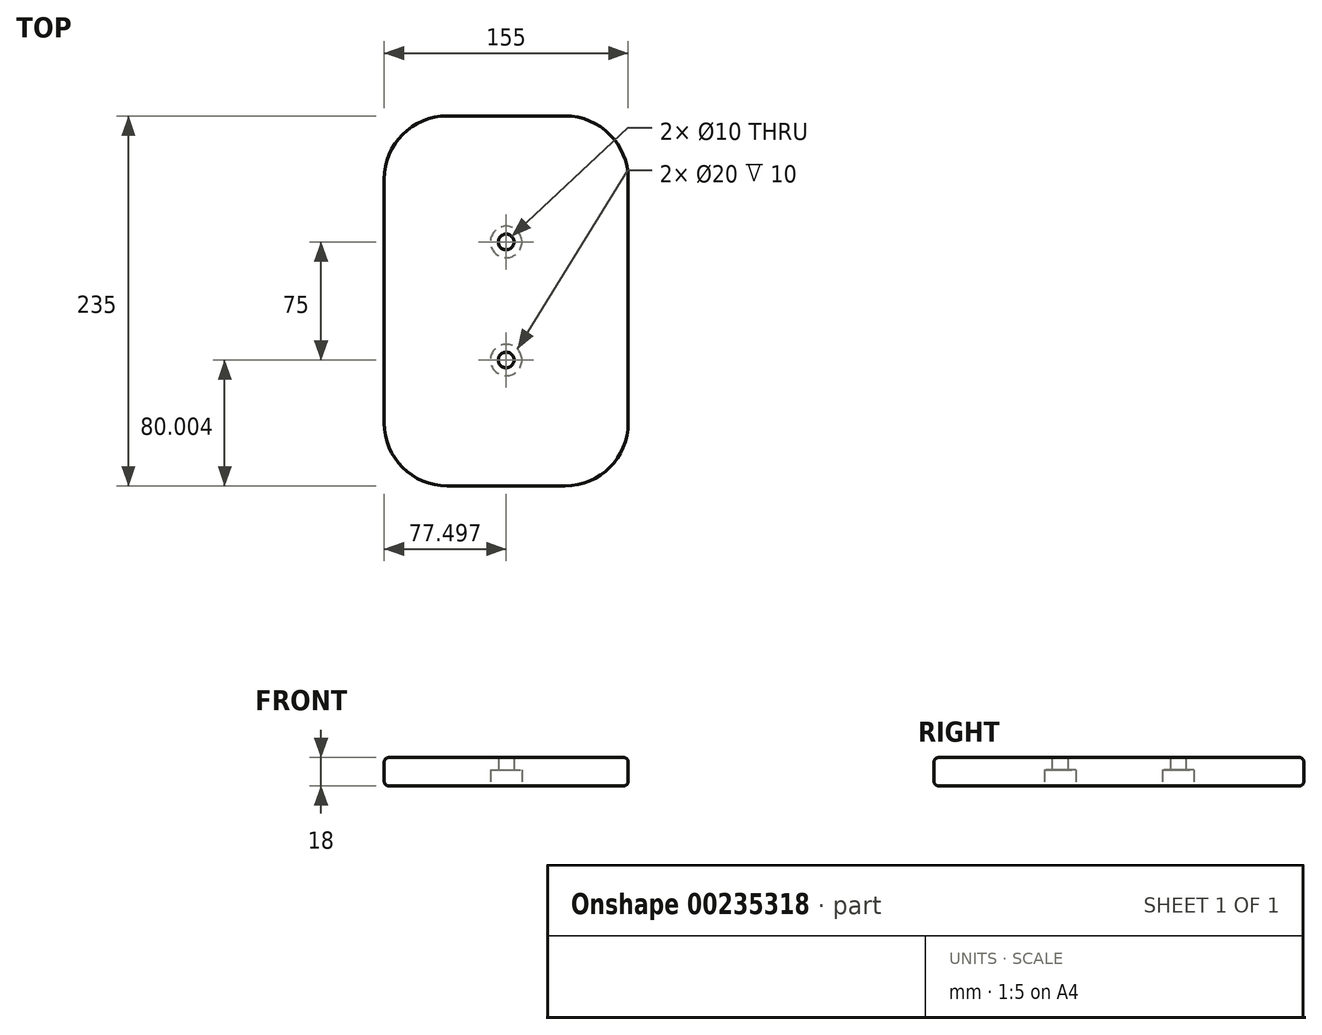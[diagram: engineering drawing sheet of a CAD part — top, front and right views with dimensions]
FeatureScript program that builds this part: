
annotation { "Feature Type Name" : "Feature", "Feature Type Description" : "" }
export const myFeature = defineFeature(function(context is Context, id is Id, definition is map)
    precondition{}
    {
        {
            var Q0;
            Q0=qCreatedBy(makeId("Top.planeOp"),FACE);
            var sketch = newSketch(context, id + "F0", { "sketchPlane" : qUnion([Q0])});
            skLineSegment(sketch, "E0.bottom", {"start": v(-32.73, -118.2) * mm, "end": v(42.27, -118.2) * mm});
            skLineSegment(sketch, "E0.top", {"start": v(-32.73, 116.8) * mm, "end": v(42.27, 116.8) * mm});
            skLineSegment(sketch, "E0.left", {"start": v(-72.73, -78.2) * mm, "end": v(-72.73, 76.8) * mm});
            skLineSegment(sketch, "E0.right", {"start": v(82.27, -78.2) * mm, "end": v(82.27, 76.8) * mm});
            skPoint(sketch, "E1.visualSharp", {"position": v(-72.73, 116.8) * mm});
            skArc(sketch, "E1.filletArc", {"start": v(-32.73, 116.8) * mm, "mid": v(-61.02, 105.09) * mm, "end": v(-72.73, 76.8) * mm});
            skPoint(sketch, "E2.visualSharp", {"position": v(82.27, 116.8) * mm});
            skArc(sketch, "E2.filletArc", {"start": v(82.27, 76.8) * mm, "mid": v(70.55, 105.09) * mm, "end": v(42.27, 116.8) * mm});
            skPoint(sketch, "E3.visualSharp", {"position": v(82.27, -118.2) * mm});
            skArc(sketch, "E3.filletArc", {"start": v(42.27, -118.2) * mm, "mid": v(70.55, -106.48) * mm, "end": v(82.27, -78.2) * mm});
            skPoint(sketch, "E4.visualSharp", {"position": v(-72.73, -118.2) * mm});
            skArc(sketch, "E4.filletArc", {"start": v(-72.73, -78.2) * mm, "mid": v(-61.02, -106.48) * mm, "end": v(-32.73, -118.2) * mm});
            skPoint(sketch, "E5.centerSnap0", {"position": v(-72.73, -0.7) * mm});
            skCircle(sketch, "E6", {"center": v(4.77, 36.8) * mm, "radius": 5 * mm});
            skPoint(sketch, "E6.centerSnap0", {"position": v(4.77, 116.8) * mm});
            skCircle(sketch, "E7", {"center": v(4.77, -38.2) * mm, "radius": 5 * mm});
            skSolve(sketch);
        }
        {
            var Q0;
            Q0=makeQuery(id+"F0.imprint","IMPRINT",FACE,{"disambiguationData":[TD([[makeQuery(id+"F0.imprint","IMPRINT",EDGE,{"derivedFrom":sQuery(id+"F0.wireOp",EDGE,"E0.bottom")}),1.0]])]});
            extrude(context, id + "F1", {"entities" : qUnion([Q0]), "depth" : 18 * mm});
        }
        {
            var Q0;
            Q0=makeQuery(id+"F1.opExtrude","CAP_FACE",FACE,{"disambiguationData":[OSD([sQuery(id+"F0.wireOp",EDGE,"E0.bottom"),sQuery(id+"F0.wireOp",EDGE,"E0.top"),sQuery(id+"F0.wireOp",EDGE,"E0.left"),sQuery(id+"F0.wireOp",EDGE,"E0.right"),sQuery(id+"F0.wireOp",EDGE,"E1.filletArc"),sQuery(id+"F0.wireOp",EDGE,"E2.filletArc"),sQuery(id+"F0.wireOp",EDGE,"E3.filletArc"),sQuery(id+"F0.wireOp",EDGE,"E4.filletArc"),sQuery(id+"F0.wireOp",EDGE,"E6"),sQuery(id+"F0.wireOp",EDGE,"E7")])],"isStart":true});
            var sketch = newSketch(context, id + "F2", { "sketchPlane" : qUnion([Q0])});
            skCircle(sketch, "E8", {"center": v(4.77, 38.2) * mm, "radius": 10 * mm});
            skCircle(sketch, "E9", {"center": v(4.77, -36.8) * mm, "radius": 10 * mm});
            skSolve(sketch);
        }
        {
            var Q0;
            Q0 = qSketchRegion(id + "F2", true);
            extrude(context, id + "F3", {"entities" : qUnion([Q0]), "operationType" : NewBodyOperationType.REMOVE, "oppositeDirection" : true, "depth" : 10 * mm});
        }
        {
            var Q0;
            Q0=makeQuery(id+"F1.opExtrude","CAP_EDGE",EDGE,{"disambiguationData":[OSD([sQuery(id+"F0.wireOp",EDGE,"E0.right")])],"isStart":false});
            var Q1;
            Q1=makeQuery(id+"F1.opExtrude","CAP_EDGE",EDGE,{"disambiguationData":[OSD([sQuery(id+"F0.wireOp",EDGE,"E0.right")])],"isStart":true});
            fillet(context, id + "F4", {"entities" : qUnion([Q0, Q1]), "radius" : 3 * mm, "tangentPropagation" : true, "allowEdgeOverflow" : false});
        }
    });
